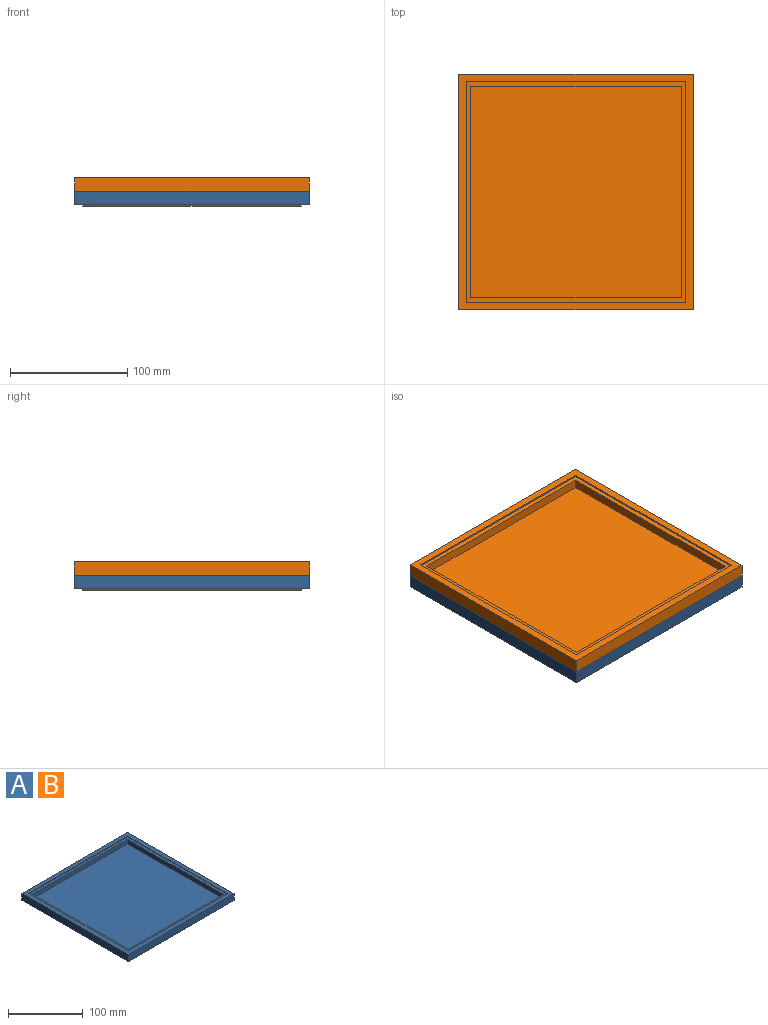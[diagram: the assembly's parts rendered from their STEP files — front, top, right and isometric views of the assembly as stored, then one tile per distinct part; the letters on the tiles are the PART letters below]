
ASSEMBLY  parts=2 mates=1
PART A: 21 faces, bbox 199.9x200.7x12.7 mm
  f0: plane 200.66x199.9mm, normal (0,0,1), area 4925.8mm2, adj f1,f2,f3,f4,f11,f12,f13,f14
  f1: plane 199.9x11.43mm, normal (0,-1,0), area 2284.8mm2, adj f0,f2,f4,f9
  f2: plane 200.66x11.43mm, normal (1,0,0), area 2293.5mm2, adj f0,f1,f3,f9
  f3: plane 199.9x11.43mm, normal (0,1,0), area 2284.8mm2, adj f0,f2,f4,f9
  f4: plane 200.66x11.43mm, normal (-1,0,0), area 2293.5mm2, adj f0,f1,f3,f9
  f5: plane 186.94x1.27mm, normal (1,0,0), area 237.4mm2, adj f6,f8,f9,f10
  f6: plane 186.18x1.27mm, normal (0,-1,0), area 236.5mm2, adj f5,f7,f9,f10
  f7: plane 186.94x1.27mm, normal (-1,0,0), area 237.4mm2, adj f6,f8,f9,f10
  f8: plane 186.18x1.27mm, normal (0,1,0), area 236.5mm2, adj f5,f7,f9,f10
  f9: plane 200.66x199.9mm, normal (0,0,-1), area 5305.9mm2, adj f1,f2,f3,f4,f5,f6,f7,f8
  f10: plane 186.94x186.18mm, normal (0,0,-1), area 34805.6mm2, adj f5,f6,f7,f8
  f11: plane 187.2x1.27mm, normal (0,1,0), area 237.7mm2, adj f0,f12,f14,f15
  f12: plane 187.96x1.27mm, normal (-1,0,0), area 238.7mm2, adj f0,f11,f13,f15
  f13: plane 187.2x1.27mm, normal (0,-1,0), area 237.7mm2, adj f0,f12,f14,f15
  f14: plane 187.96x1.27mm, normal (1,0,0), area 238.7mm2, adj f0,f11,f13,f15
  f15: plane 187.96x187.2mm, normal (0,0,1), area 2800.6mm2, adj f11,f12,f13,f14,f17,f18,f19,f20
  f16: plane 180.34x179.58mm, normal (0,0,1), area 32385.1mm2, adj f17,f18,f19,f20
  f17: plane 180.34x7.62mm, normal (1,0,0), area 1374.2mm2, adj f15,f16,f18,f20
  f18: plane 179.58x7.62mm, normal (0,-1,0), area 1368.4mm2, adj f15,f16,f17,f19
  f19: plane 180.34x7.62mm, normal (-1,0,0), area 1374.2mm2, adj f15,f16,f18,f20
  f20: plane 179.58x7.62mm, normal (0,1,0), area 1368.4mm2, adj f15,f16,f17,f19
PART B: same geometry as A
PLACE A t=(0,0,-48.77)mm
PLACE B t=(0,0,-37.34)mm
MATE fastened B.f9 <-> A.f0  axis (0,0,-1) through (99.95,-100.33,-36.07)mm
